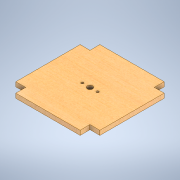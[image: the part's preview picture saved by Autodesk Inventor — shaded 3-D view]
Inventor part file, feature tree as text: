
AUTODESK INVENTOR PART (.ipt)
format: ipt  version: 2021 (Build 250183000, 183)  size: 149,504 bytes
history: native  units: mm
features: sketch x4, extrude x2, hole x2, other x1, pattern_circular x1
ambient origin geometry x8: Origin, YZ Plane, XZ Plane, XY Plane, X Axis, Y Axis, Z Axis, Center Point
bodies: Body1 (feature_tree)
feature tree (10):
  other  "實體1"
  extrude  "擠出1"  Depth=170.0mm
  extrude  "擠出2"  Depth=170.0mm
  pattern_circular  "環形陣列1"  [2 undecoded]
  hole  "孔3"  [1 undecoded]
  hole  "孔4"  [1 undecoded]
  sketch  "草圖1"
  sketch  "草圖2"
  sketch  "草圖5"
  sketch  "草圖6"
note: 4 required parameter values undecoded (feature->parameter linkage not recoverable at this tier; creation-order binding heuristic only, values carry confidence <= 0.55)
